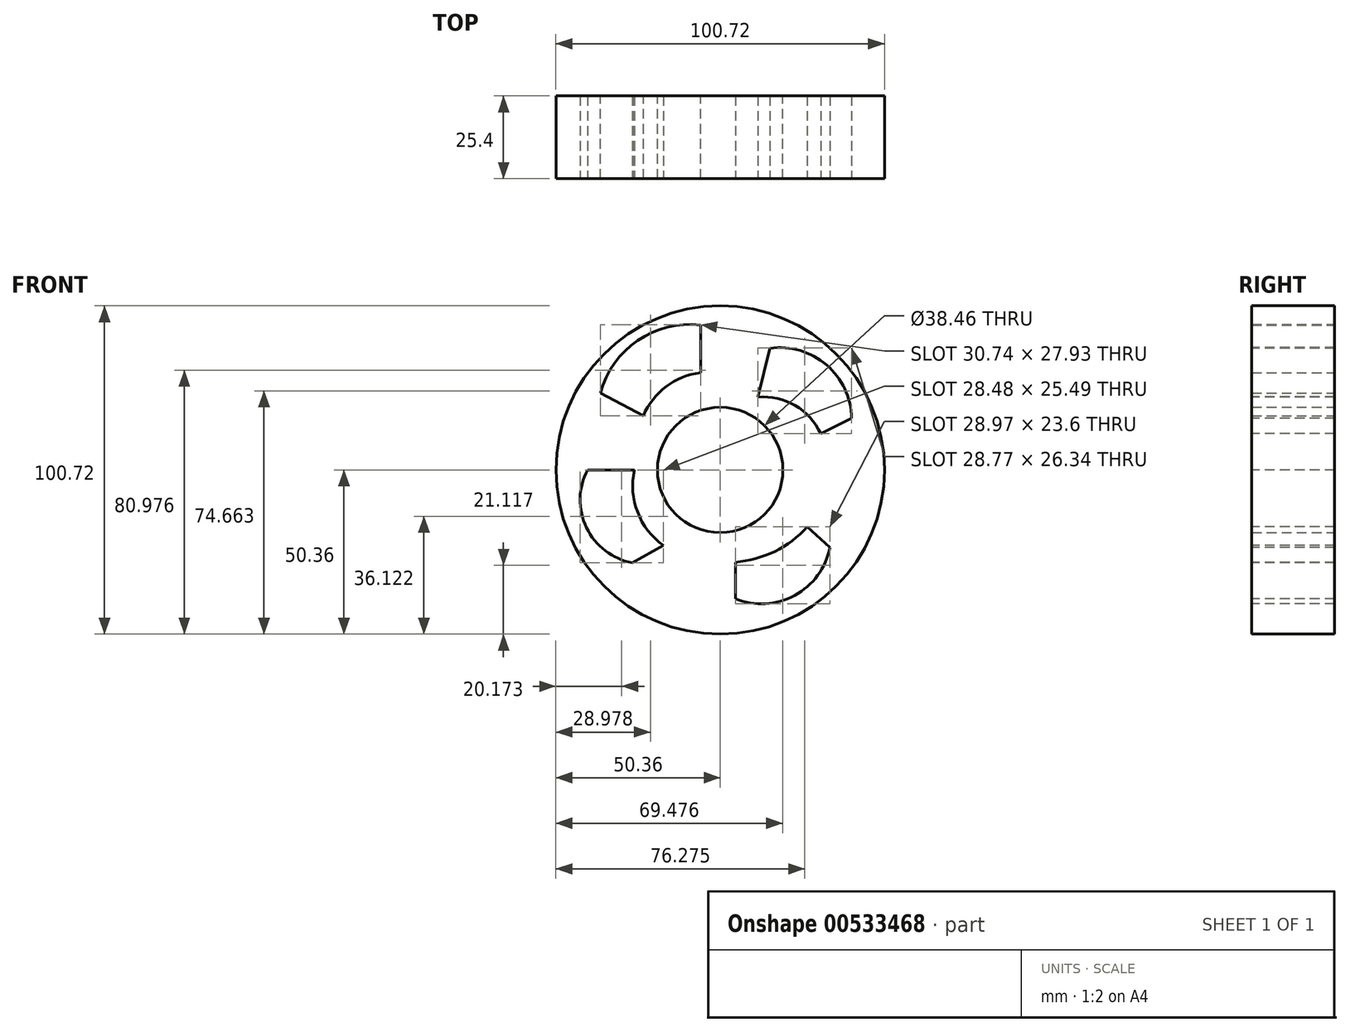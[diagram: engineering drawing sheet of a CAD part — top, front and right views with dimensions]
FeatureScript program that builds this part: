
annotation { "Feature Type Name" : "Feature", "Feature Type Description" : "" }
export const myFeature = defineFeature(function(context is Context, id is Id, definition is map)
    precondition{}
    {
        {
            var Q0;
            Q0=qCreatedBy(makeId("Front.planeOp"),FACE);
            var sketch = newSketch(context, id + "F0", { "sketchPlane" : qUnion([Q0])});
            skCircle(sketch, "E0", {"center": v(0, 0) * mm, "radius": 50.36 * mm});
            skCircle(sketch, "E1", {"center": v(0, 0) * mm, "radius": 19.23 * mm});
            skSolve(sketch);
        }
        {
            var Q0;
            Q0=makeQuery(id+"F0.imprint","IMPRINT",FACE,{"disambiguationData":[TD([[makeQuery(id+"F0.imprint","IMPRINT",EDGE,{"derivedFrom":sQuery(id+"F0.wireOp",EDGE,"E0")}),1.0]])]});
            var sketch = newSketch(context, id + "F1", { "sketchPlane" : qUnion([Q0])});
            skLineSegment(sketch, "E2", {"start": v(-36.75, 23.55) * mm, "end": v(-23.55, 16.65) * mm});
            skArc(sketch, "E3", {"start": v(-6.01, 44.44) * mm, "mid": v(-25.28, 39.73) * mm, "end": v(-36.75, 23.55) * mm});
            skLineSegment(sketch, "E4", {"start": v(-6.01, 44.44) * mm, "end": v(-6.01, 29.86) * mm});
            skArc(sketch, "E5", {"start": v(-6.01, 29.86) * mm, "mid": v(-16.55, 25.6) * mm, "end": v(-23.55, 16.65) * mm});
            skSolve(sketch);
        }
        {
            var Q0;
            Q0=makeQuery(id+"F0.imprint","IMPRINT",FACE,{"disambiguationData":[TD([[makeQuery(id+"F0.imprint","IMPRINT",EDGE,{"derivedFrom":sQuery(id+"F0.wireOp",EDGE,"E0")}),1.0]])]});
            extrude(context, id + "F2", {"entities" : qUnion([Q0]), "depth" : 25.4 * mm, "offsetDistance" : 25.4 * mm});
        }
        {
            var Q0;
            Q0=makeQuery(id+"F1.imprint","IMPRINT",FACE,{"disambiguationData":[TD([[makeQuery(id+"F1.imprint","IMPRINT",EDGE,{"derivedFrom":sQuery(id+"F1.wireOp",EDGE,"E2")}),1.0]])]});
            extrude(context, id + "F3", {"entities" : qUnion([Q0]), "operationType" : NewBodyOperationType.REMOVE, "depth" : 159.5 * mm, "offsetDistance" : 25.4 * mm});
        }
        {
            var Q0;
            Q0=makeQuery(id+"F2.opExtrude","CAP_FACE",FACE,{"disambiguationData":[OSD([sQuery(id+"F0.wireOp",EDGE,"E0"),sQuery(id+"F0.wireOp",EDGE,"E1")])],"isStart":false});
            var sketch = newSketch(context, id + "F4", { "sketchPlane" : qUnion([Q0])});
            skLineSegment(sketch, "E6", {"start": v(-26.3, 0) * mm, "end": v(-40.7, 0) * mm});
            skArc(sketch, "E7", {"start": v(-40.7, 0) * mm, "mid": v(-40.97, -17.71) * mm, "end": v(-26.9, -28.48) * mm});
            skLineSegment(sketch, "E8", {"start": v(-26.9, -28.48) * mm, "end": v(-17.44, -23.16) * mm});
            skArc(sketch, "E9", {"start": v(-26.3, 0) * mm, "mid": v(-25.34, -12.9) * mm, "end": v(-17.44, -23.16) * mm});
            skSolve(sketch);
        }
        {
            var Q0;
            Q0=makeQuery(id+"F4.imprint","IMPRINT",FACE,{"disambiguationData":[TD([[makeQuery(id+"F4.imprint","IMPRINT",EDGE,{"derivedFrom":sQuery(id+"F4.wireOp",EDGE,"E6")}),-1.0]])]});
            var sketch = newSketch(context, id + "F5", { "sketchPlane" : qUnion([Q0])});
            skLineSegment(sketch, "E10", {"start": v(4.63, -28.28) * mm, "end": v(4.63, -39.51) * mm});
            skArc(sketch, "E11", {"start": v(4.63, -39.51) * mm, "mid": v(22.85, -38.48) * mm, "end": v(33.6, -23.75) * mm});
            skLineSegment(sketch, "E12", {"start": v(33.6, -23.75) * mm, "end": v(26.7, -17.44) * mm});
            skArc(sketch, "E13", {"start": v(4.63, -28.28) * mm, "mid": v(16.7, -24.98) * mm, "end": v(26.7, -17.44) * mm});
            skLineSegment(sketch, "E14", {"start": v(11.53, 22.37) * mm, "end": v(15.27, 37.34) * mm});
            skArc(sketch, "E15", {"start": v(40.3, 15.86) * mm, "mid": v(32.6, 32.2) * mm, "end": v(15.27, 37.34) * mm});
            skLineSegment(sketch, "E16", {"start": v(40.3, 15.86) * mm, "end": v(30.84, 11.13) * mm});
            skArc(sketch, "E17", {"start": v(30.84, 11.13) * mm, "mid": v(22.95, 19.79) * mm, "end": v(11.53, 22.37) * mm});
            skSolve(sketch);
        }
        {
            var Q0;
            Q0=makeQuery(id+"F4.imprint","IMPRINT",FACE,{"disambiguationData":[TD([[makeQuery(id+"F4.imprint","IMPRINT",EDGE,{"derivedFrom":sQuery(id+"F4.wireOp",EDGE,"E6")}),1.0]])]});
            extrude(context, id + "F6", {"entities" : qUnion([Q0]), "operationType" : NewBodyOperationType.REMOVE, "oppositeDirection" : true, "depth" : 39.62 * mm, "offsetDistance" : 25.4 * mm});
        }
        {
            var Q0;
            Q0=makeQuery(id+"F5.imprint","IMPRINT",FACE,{"disambiguationData":[TD([[makeQuery(id+"F5.imprint","IMPRINT",EDGE,{"derivedFrom":sQuery(id+"F5.wireOp",EDGE,"E14")}),-1.0]])]});
            var Q1;
            Q1=makeQuery(id+"F5.imprint","IMPRINT",FACE,{"disambiguationData":[TD([[makeQuery(id+"F5.imprint","IMPRINT",EDGE,{"derivedFrom":sQuery(id+"F5.wireOp",EDGE,"E10")}),1.0]])]});
            extrude(context, id + "F7", {"entities" : qUnion([Q0, Q1]), "operationType" : NewBodyOperationType.REMOVE, "oppositeDirection" : true, "depth" : 60.45 * mm, "offsetDistance" : 25.4 * mm});
        }
    });
